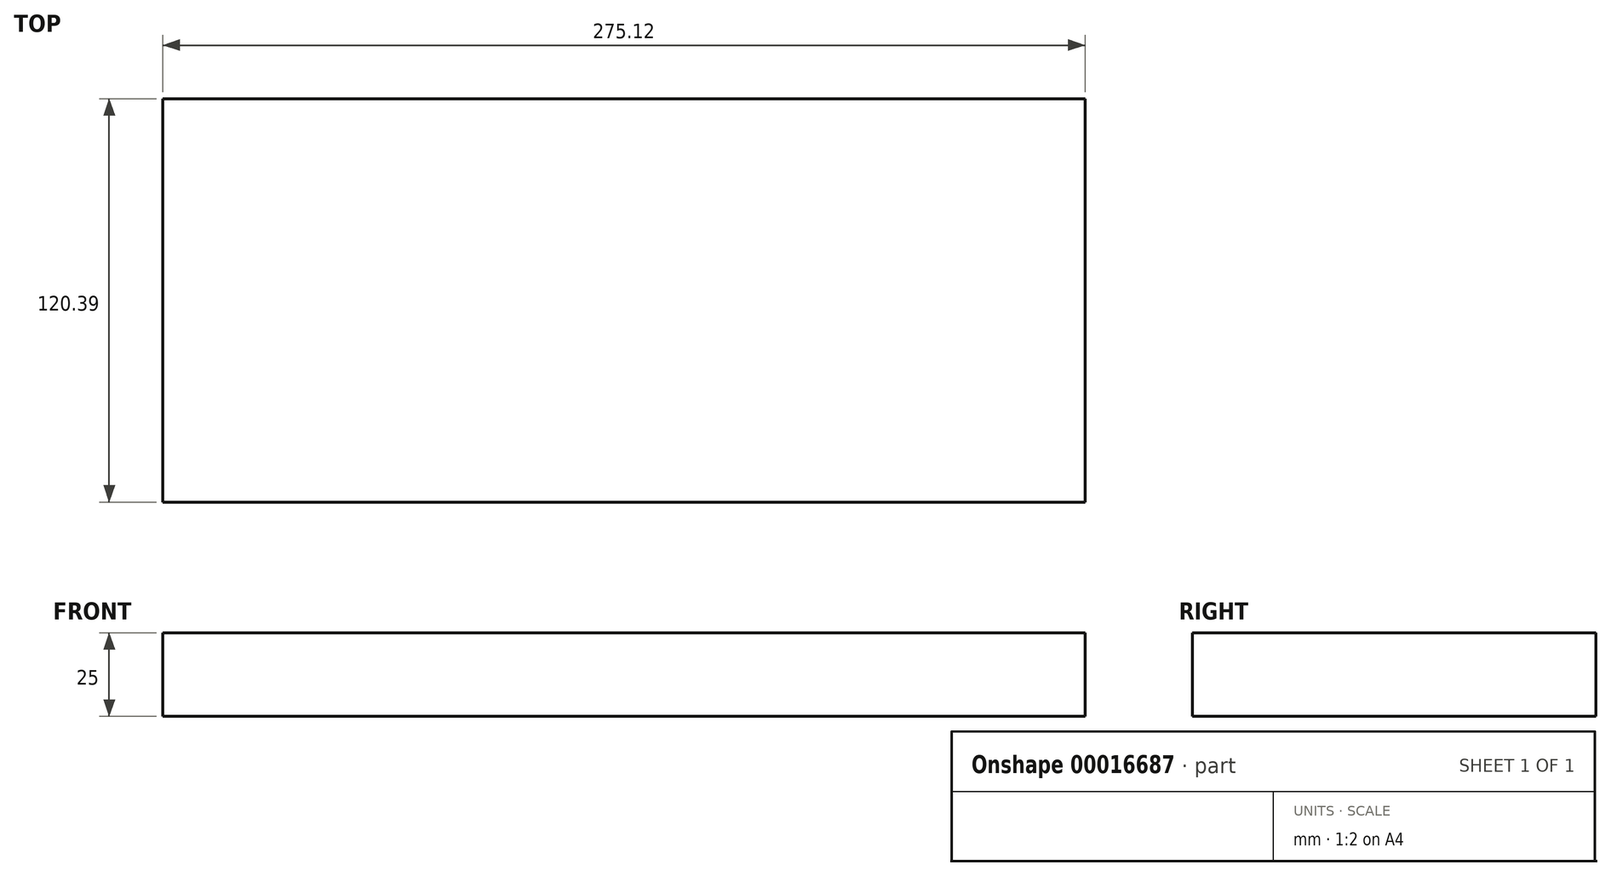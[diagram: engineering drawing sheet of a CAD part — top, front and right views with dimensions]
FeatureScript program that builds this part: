
annotation { "Feature Type Name" : "Feature", "Feature Type Description" : "" }
export const myFeature = defineFeature(function(context is Context, id is Id, definition is map)
    precondition{}
    {
        {
            var Q0;
            Q0=qCreatedBy(makeId("Top.planeOp"),FACE);
            var sketch = newSketch(context, id + "F0", { "sketchPlane" : qUnion([Q0])});
            skLineSegment(sketch, "E0.bottom", {"start": v(-137.65, 65.62) * mm, "end": v(137.47, 65.62) * mm});
            skLineSegment(sketch, "E0.top", {"start": v(-137.65, -54.77) * mm, "end": v(137.47, -54.77) * mm});
            skLineSegment(sketch, "E0.left", {"start": v(-137.65, 65.62) * mm, "end": v(-137.65, -54.77) * mm});
            skLineSegment(sketch, "E0.right", {"start": v(137.47, 65.62) * mm, "end": v(137.47, -54.77) * mm});
            skSolve(sketch);
        }
        {
            var Q0;
            Q0=makeQuery(id+"F0.imprint","IMPRINT",FACE,{"disambiguationData":[TD([[makeQuery(id+"F0.imprint","IMPRINT",EDGE,{"derivedFrom":sQuery(id+"F0.wireOp",EDGE,"E0.bottom")}),-1.0]])]});
            extrude(context, id + "F1", {"entities" : qUnion([Q0]), "depth" : 25 * mm});
        }
    });
